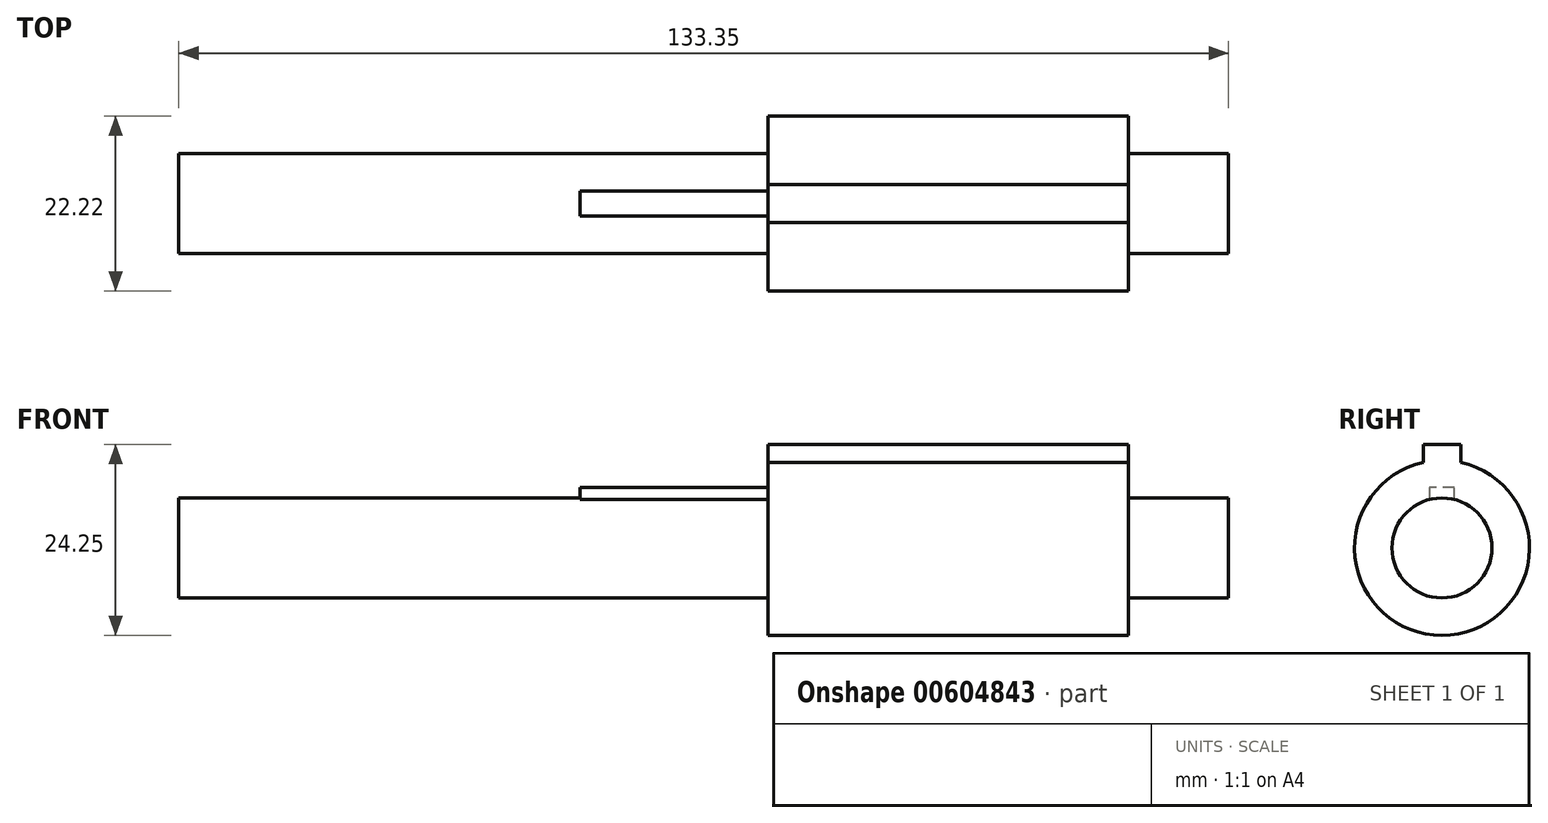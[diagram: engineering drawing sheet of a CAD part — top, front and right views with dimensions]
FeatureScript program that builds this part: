
annotation { "Feature Type Name" : "Feature", "Feature Type Description" : "" }
export const myFeature = defineFeature(function(context is Context, id is Id, definition is map)
    precondition{}
    {
        {
            var Q0;
            Q0=qCreatedBy(makeId("Front.planeOp"),FACE);
            var sketch = newSketch(context, id + "F0", { "sketchPlane" : qUnion([Q0])});
            skLineSegment(sketch, "E0.bottom", {"start": v(0, 0) * mm, "end": v(133.35, 0) * mm});
            skLineSegment(sketch, "E0.top", {"start": v(0, 6.35) * mm, "end": v(133.35, 6.35) * mm});
            skLineSegment(sketch, "E0.left", {"start": v(0, 0) * mm, "end": v(0, 6.35) * mm});
            skLineSegment(sketch, "E0.right", {"start": v(133.35, 0) * mm, "end": v(133.35, 6.35) * mm});
            skLineSegment(sketch, "E1.bottom", {"start": v(120.65, 0) * mm, "end": v(74.83, 0) * mm});
            skLineSegment(sketch, "E1.top", {"start": v(120.65, 11.11) * mm, "end": v(74.83, 11.11) * mm});
            skLineSegment(sketch, "E1.left", {"start": v(120.65, 0) * mm, "end": v(120.65, 11.11) * mm});
            skLineSegment(sketch, "E1.right", {"start": v(74.83, 0) * mm, "end": v(74.83, 11.11) * mm});
            skLineSegment(sketch, "E2", {"start": v(120.65, 0) * mm, "end": v(133.35, 0) * mm});
            skSolve(sketch);
        }
        {
            var Q0;
            {var subQ0=sQuery(id+"F0.wireOp",EDGE,"E0.bottom");Q0=makeQuery(id+"F0.imprint","IMPRINT",FACE,{"disambiguationData":[TD([[makeQuery(id+"F0.imprint","IMPRINT",EDGE,{"derivedFrom":subQ0}),1.0]])]});}
            var Q1;
            {var subQ5=sQuery(id+"F0.wireOp",EDGE,"E1.bottom");Q1=makeQuery(id+"F0.imprint","IMPRINT",FACE,{"disambiguationData":[TD([[makeQuery(id+"F0.imprint","IMPRINT",EDGE,{"derivedFrom":subQ5}),-1.0]])]});}
            var Q2;
            {var subQ5=sQuery(id+"F0.wireOp",EDGE,"E1.top");Q2=makeQuery(id+"F0.imprint","IMPRINT",FACE,{"disambiguationData":[TD([[makeQuery(id+"F0.imprint","IMPRINT",EDGE,{"derivedFrom":subQ5}),1.0]])]});}
            var Q3;
            {var subQ0=sQuery(id+"F0.wireOp",EDGE,"E0.right");Q3=makeQuery(id+"F0.imprint","IMPRINT",FACE,{"disambiguationData":[TD([[makeQuery(id+"F0.imprint","IMPRINT",EDGE,{"derivedFrom":subQ0}),1.0]])]});}
            var Q4;
            Q4=sQuery(id+"F0.wireOp",EDGE,"E0.bottom");
            revolve(context, id + "F1", {"entities" : qUnion([Q0, Q1, Q2, Q3]), "axis" : qUnion([Q4]), "revolveType" : RevolveType.FULL});
        }
        {
            var Q0;
            Q0=makeQuery(id+"F1.opRevolve","SWEPT_FACE",FACE,{"disambiguationData":[OSD([sQuery(id+"F0.wireOp",EDGE,"E1.left")])]});
            var sketch = newSketch(context, id + "F2", { "sketchPlane" : qUnion([Q0])});
            skLineSegment(sketch, "E3", {"start": v(-2.39, 10.85) * mm, "end": v(2.39, 10.85) * mm});
            skLineSegment(sketch, "E4", {"start": v(-2.39, 10.85) * mm, "end": v(-2.39, 13.14) * mm});
            skLineSegment(sketch, "E5", {"start": v(-2.39, 13.14) * mm, "end": v(2.39, 13.14) * mm});
            skLineSegment(sketch, "E6", {"start": v(2.39, 13.14) * mm, "end": v(2.39, 10.85) * mm});
            skSolve(sketch);
        }
        {
            var Q0;
            {var subQ0=sQuery(id+"F2.wireOp",EDGE,"E4");Q0=makeQuery(id+"F2.imprint","IMPRINT",FACE,{"disambiguationData":[TD([[makeQuery(id+"F2.imprint","IMPRINT",EDGE,{"derivedFrom":subQ0}),-1.0]])]});}
            extrude(context, id + "F3", {"entities" : qUnion([Q0]), "operationType" : NewBodyOperationType.ADD, "oppositeDirection" : true, "depth" : 45.82 * mm, "offsetDistance" : 25 * mm});
        }
        {
            var Q0;
            Q0=makeQuery(id+"F1.opRevolve","SWEPT_FACE",FACE,{"disambiguationData":[OSD([sQuery(id+"F0.wireOp",EDGE,"E1.right")])]});
            var sketch = newSketch(context, id + "F4", { "sketchPlane" : qUnion([Q0])});
            skLineSegment(sketch, "E7", {"start": v(-1.59, 6.15) * mm, "end": v(1.59, 6.15) * mm});
            skLineSegment(sketch, "E8", {"start": v(-1.59, 6.15) * mm, "end": v(-1.59, 7.67) * mm});
            skLineSegment(sketch, "E9", {"start": v(-1.59, 7.67) * mm, "end": v(1.59, 7.67) * mm});
            skLineSegment(sketch, "E10", {"start": v(1.59, 7.67) * mm, "end": v(1.59, 6.15) * mm});
            skSolve(sketch);
        }
        {
            var Q0;
            {var subQ0=sQuery(id+"F4.wireOp",EDGE,"E8");Q0=makeQuery(id+"F4.imprint","IMPRINT",FACE,{"disambiguationData":[TD([[makeQuery(id+"F4.imprint","IMPRINT",EDGE,{"derivedFrom":subQ0}),-1.0]])]});}
            extrude(context, id + "F5", {"entities" : qUnion([Q0]), "operationType" : NewBodyOperationType.ADD, "depth" : 23.83 * mm, "offsetDistance" : 25 * mm});
        }
    });
